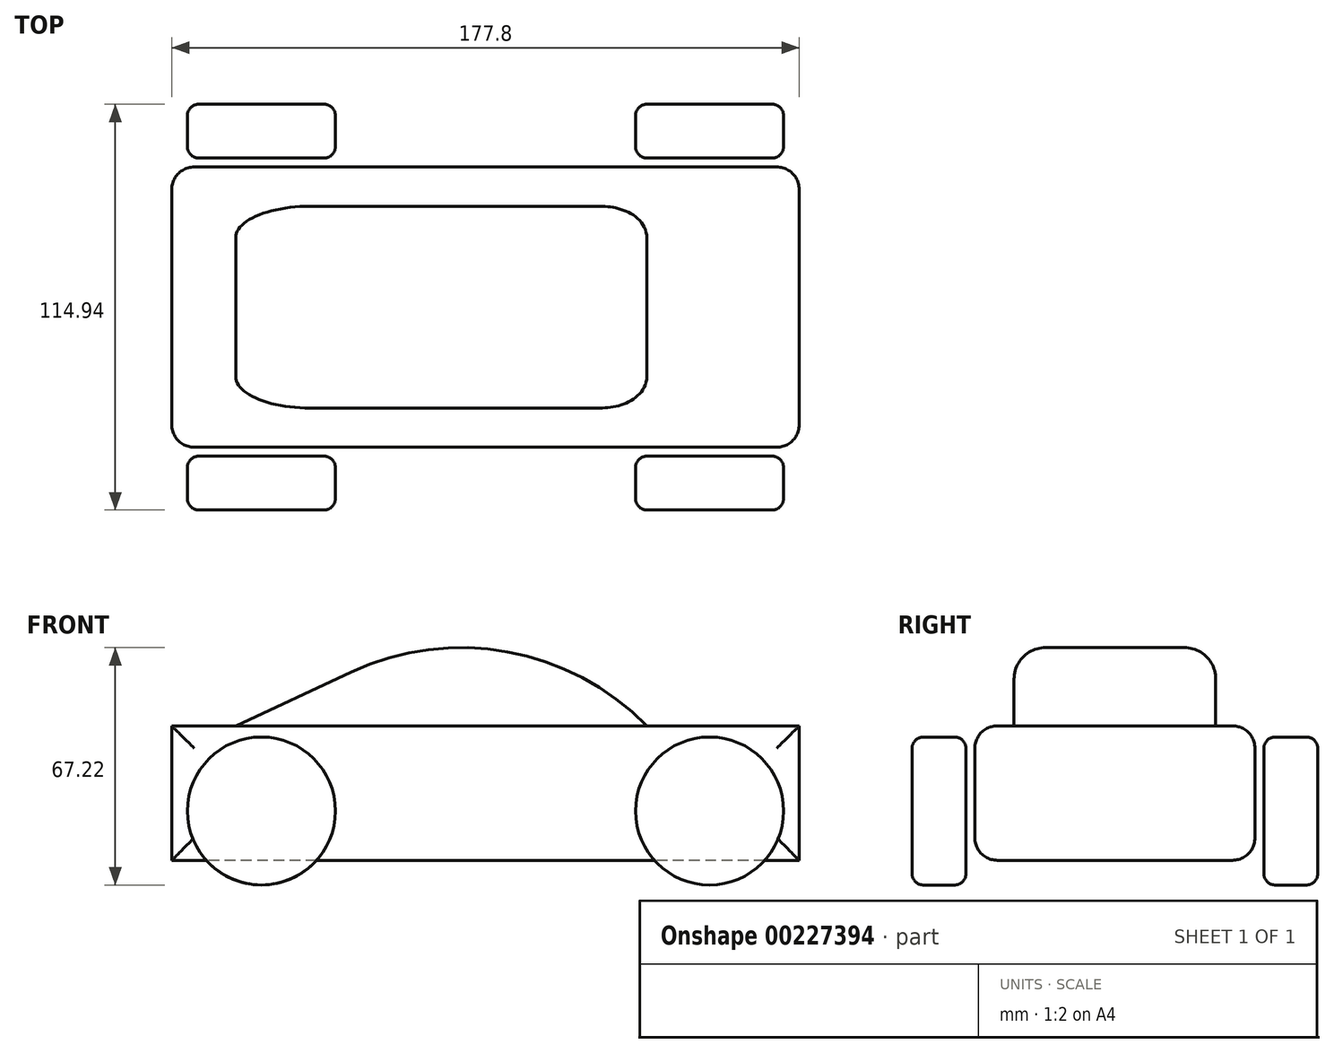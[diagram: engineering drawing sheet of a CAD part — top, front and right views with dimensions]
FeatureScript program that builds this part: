
annotation { "Feature Type Name" : "Feature", "Feature Type Description" : "" }
export const myFeature = defineFeature(function(context is Context, id is Id, definition is map)
    precondition{}
    {
        {
            var Q0;
            Q0=qCreatedBy(makeId("Front.planeOp"),FACE);
            var sketch = newSketch(context, id + "F0", { "sketchPlane" : qUnion([Q0])});
            skLineSegment(sketch, "E0.bottom", {"start": v(88.9, 19.05) * mm, "end": v(-88.9, 19.05) * mm});
            skLineSegment(sketch, "E0.top", {"start": v(88.9, -19.05) * mm, "end": v(-88.9, -19.05) * mm});
            skLineSegment(sketch, "E0.left", {"start": v(88.9, 19.05) * mm, "end": v(88.9, -19.05) * mm});
            skLineSegment(sketch, "E0.right", {"start": v(-88.9, 19.05) * mm, "end": v(-88.9, -19.05) * mm});
            skPoint(sketch, "E0.middle", {"position": v(0, 0) * mm});
            skLineSegment(sketch, "E1", {"start": v(-99.97, -26.04) * mm, "end": v(102.96, -26.03) * mm, "construction": true});
            skCircle(sketch, "E2", {"center": v(63.5, -5.08) * mm, "radius": 20.96 * mm});
            skSolve(sketch);
        }
        {
            var Q0;
            Q0=qCreatedBy(makeId("Front.planeOp"),FACE);
            var sketch = newSketch(context, id + "F1", { "sketchPlane" : qUnion([Q0])});
            skLineSegment(sketch, "E3.0", {"start": v(-88.9, 19.05) * mm, "end": v(-88.9, -19.05) * mm});
            skLineSegment(sketch, "E4.0", {"start": v(88.9, 19.05) * mm, "end": v(-88.9, 19.05) * mm});
            skLineSegment(sketch, "E5.0", {"start": v(88.9, 19.05) * mm, "end": v(88.9, -19.05) * mm});
            skLineSegment(sketch, "E6.0", {"start": v(88.9, -19.05) * mm, "end": v(-88.9, -19.05) * mm});
            skSolve(sketch);
        }
        {
            var Q0;
            Q0 = qSketchRegion(id + "F1", true);
            extrude(context, id + "F2", {"entities" : qUnion([Q0]), "endBound" : BoundingType.SYMMETRIC, "depth" : 79.38 * mm});
        }
        {
            var Q0;
            Q0=makeQuery(id+"F2.opExtrude","CAP_FACE",FACE,{"disambiguationData":[OSD([sQuery(id+"F1.wireOp",EDGE,"E3.0"),sQuery(id+"F1.wireOp",EDGE,"E4.0"),sQuery(id+"F1.wireOp",EDGE,"E5.0"),sQuery(id+"F1.wireOp",EDGE,"E6.0")])],"isStart":false});
            cPlane(context, id + "F3", {"entities" : qUnion([Q0]), "cplaneType" : CPlaneType.OFFSET, "offset" : 2.54 * mm, "width" : 152.4 * mm, "height" : 152.4 * mm});
        }
        {
            var Q0;
            Q0=qCreatedBy(id+"F3.planeOp",FACE);
            var sketch = newSketch(context, id + "F4", { "sketchPlane" : qUnion([Q0])});
            skCircle(sketch, "E7.0", {"center": v(63.5, -5.08) * mm, "radius": 20.96 * mm});
            skSolve(sketch);
        }
        {
            var Q0;
            Q0 = qSketchRegion(id + "F4", true);
            extrude(context, id + "F5", {"entities" : qUnion([Q0]), "depth" : 15.24 * mm});
        }
        {
            var Q0;
            Q0=makeQuery(id+"F5.opExtrude","CAP_EDGE",EDGE,{"disambiguationData":[OSD([sQuery(id+"F4.wireOp",EDGE,"E7.0")])],"isStart":false});
            var Q1;
            Q1=makeQuery(id+"F5.opExtrude","CAP_EDGE",EDGE,{"disambiguationData":[OSD([sQuery(id+"F4.wireOp",EDGE,"E7.0")])],"isStart":true});
            fillet(context, id + "F6", {"entities" : qUnion([Q0, Q1]), "radius" : 3.17 * mm, "tangentPropagation" : true, "allowEdgeOverflow" : false});
        }
        {
            var Q0;
            Q0=makeQuery(id+"F2.opExtrude","CAP_FACE",FACE,{"disambiguationData":[OSD([sQuery(id+"F1.wireOp",EDGE,"E3.0"),sQuery(id+"F1.wireOp",EDGE,"E4.0"),sQuery(id+"F1.wireOp",EDGE,"E5.0"),sQuery(id+"F1.wireOp",EDGE,"E6.0")])],"isStart":false});
            var Q1;
            Q1=makeQuery(id+"F2.opExtrude","CAP_FACE",FACE,{"disambiguationData":[OSD([sQuery(id+"F1.wireOp",EDGE,"E3.0"),sQuery(id+"F1.wireOp",EDGE,"E4.0"),sQuery(id+"F1.wireOp",EDGE,"E5.0"),sQuery(id+"F1.wireOp",EDGE,"E6.0")])],"isStart":true});
            fillet(context, id + "F7", {"entities" : qUnion([Q0, Q1]), "radius" : 6.35 * mm, "tangentPropagation" : true, "allowEdgeOverflow" : false});
        }
        {
            var Q0;
            Q0=makeQuery(id+"F5.opExtrude","SWEPT_BODY",BODY,{"disambiguationData":[OSD([sQuery(id+"F4.wireOp",EDGE,"E7.0")])]});
            var Q1;
            Q1=qCreatedBy(makeId("Front.planeOp"),FACE);
            mirror(context, id + "F8", {"entities" : qUnion([Q0]), "mirrorPlane" : qUnion([Q1])});
        }
        {
            var Q0;
            Q0=makeQuery(id+"F5.opExtrude","SWEPT_BODY",BODY,{"disambiguationData":[OSD([sQuery(id+"F4.wireOp",EDGE,"E7.0")])]});
            var Q1;
            Q1=makeQuery(id+"F8.opPattern","COPY",BODY,{"derivedFrom":makeQuery(id+"F5.opExtrude","SWEPT_BODY",BODY,{"disambiguationData":[OSD([sQuery(id+"F4.wireOp",EDGE,"E7.0")])]}),"instanceName":"1"});
            var Q2;
            Q2=qCreatedBy(makeId("Right.planeOp"),FACE);
            mirror(context, id + "F9", {"entities" : qUnion([Q0, Q1]), "mirrorPlane" : qUnion([Q2])});
        }
        {
            var Q0;
            Q0=qCreatedBy(makeId("Front.planeOp"),FACE);
            var sketch = newSketch(context, id + "F10", { "sketchPlane" : qUnion([Q0])});
            skLineSegment(sketch, "E8", {"start": v(-70.75, 19.05) * mm, "end": v(-38.1, 34.28) * mm});
            skArc(sketch, "E9", {"start": v(45.72, 19.05) * mm, "mid": v(6.23, 40) * mm, "end": v(-38.1, 34.28) * mm});
            skPoint(sketch, "E10.orphan", {"position": v(-88.9, 19.05) * mm});
            skPoint(sketch, "E11.orphan", {"position": v(88.9, 19.05) * mm});
            skLineSegment(sketch, "E12", {"start": v(-70.75, 19.05) * mm, "end": v(45.72, 19.05) * mm});
            skSolve(sketch);
        }
        {
            var Q0;
            Q0 = qSketchRegion(id + "F10", true);
            extrude(context, id + "F11", {"entities" : qUnion([Q0]), "endBound" : BoundingType.SYMMETRIC, "depth" : 57.15 * mm});
        }
        {
            var Q0;
            Q0=makeQuery(id+"F11.opExtrude","CAP_EDGE",EDGE,{"disambiguationData":[OSD([sQuery(id+"F10.wireOp",EDGE,"E9")])],"isStart":false});
            var Q1;
            Q1=makeQuery(id+"F11.opExtrude","CAP_EDGE",EDGE,{"disambiguationData":[OSD([sQuery(id+"F10.wireOp",EDGE,"E9")])],"isStart":true});
            fillet(context, id + "F12", {"entities" : qUnion([Q0, Q1]), "radius" : 8.9 * mm, "tangentPropagation" : true, "allowEdgeOverflow" : false});
        }
    });
